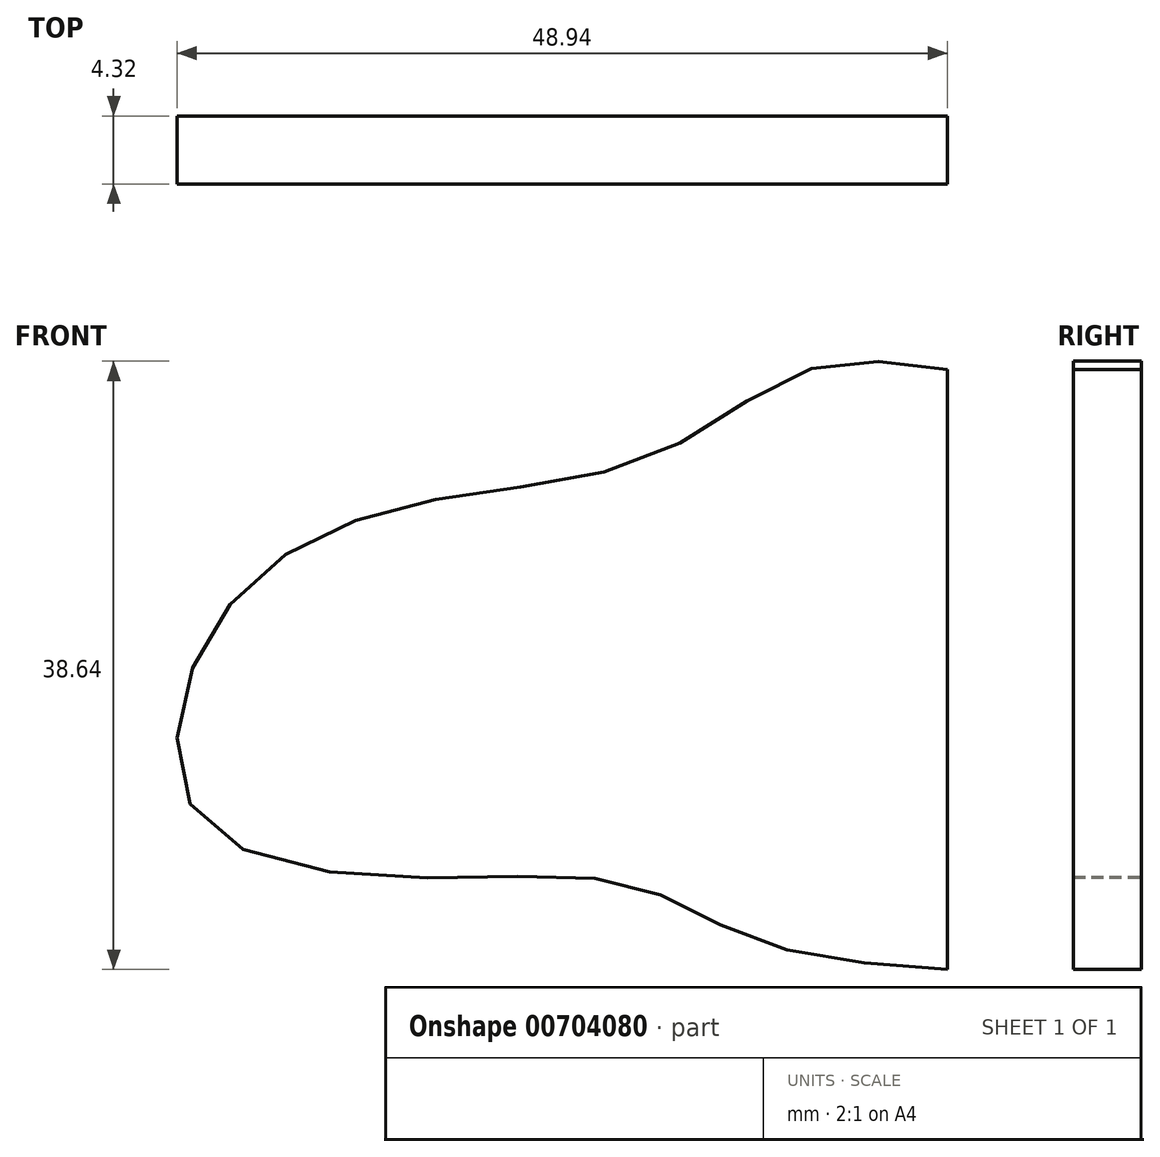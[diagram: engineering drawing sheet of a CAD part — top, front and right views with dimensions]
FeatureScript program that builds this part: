
annotation { "Feature Type Name" : "Feature", "Feature Type Description" : "" }
export const myFeature = defineFeature(function(context is Context, id is Id, definition is map)
    precondition{}
    {
        {
            var Q0;
            Q0=qCreatedBy(makeId("Front.planeOp"),FACE);
            var sketch = newSketch(context, id + "F0", { "sketchPlane" : qUnion([Q0])});
            skFitSpline(sketch, "E0", {"points": [v(0, 0) * mm, v(-8.83, 0) * mm, v(-18.66, -5.48) * mm, v(-32.07, -8.16) * mm, v(-43.25, -12.63) * mm, v(-48.61, -21.12) * mm, v(-46.82, -29.17) * mm, v(-32.07, -32.3) * mm, v(-20, -32.74) * mm, v(-11.96, -36.32) * mm, v(0, -38.1) * mm], "startDerivative": vector(-100.95, 15.8) * mm, "endDerivative": vector(122.69, -7.96) * mm});
            skLineSegment(sketch, "E1", {"start": v(0, -38.1) * mm, "end": v(0, 0) * mm});
            skSolve(sketch);
        }
        {
            var Q0;
            Q0=makeQuery(id+"F0.imprint","IMPRINT",FACE,{"disambiguationData":[TD([[makeQuery(id+"F0.imprint","IMPRINT",EDGE,{"derivedFrom":sQuery(id+"F0.wireOp",EDGE,"E0")}),1.0]])]});
            extrude(context, id + "F1", {"entities" : qUnion([Q0]), "depth" : 4.32 * mm, "offsetDistance" : 25.4 * mm});
        }
    });
